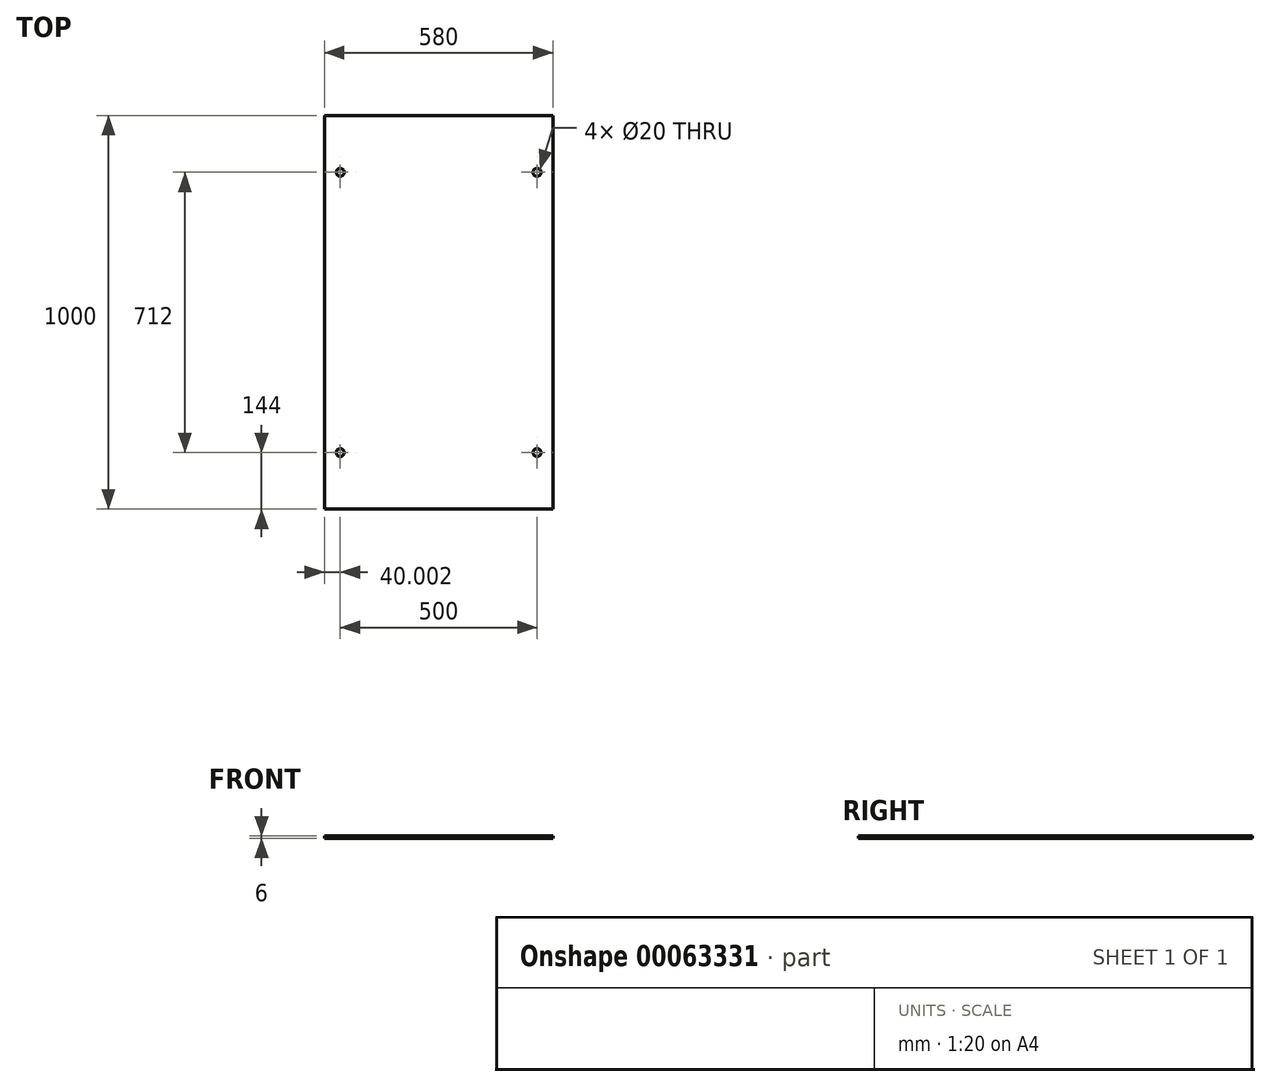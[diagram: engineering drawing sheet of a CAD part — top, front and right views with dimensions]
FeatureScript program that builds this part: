
annotation { "Feature Type Name" : "Feature", "Feature Type Description" : "" }
export const myFeature = defineFeature(function(context is Context, id is Id, definition is map)
    precondition{}
    {
        {
            var Q0;
            Q0=qCreatedBy(makeId("Top.planeOp"),FACE);
            var sketch = newSketch(context, id + "F0", { "sketchPlane" : qUnion([Q0])});
            skLineSegment(sketch, "E0.rect.bottom", {"start": v(293.63, -500) * mm, "end": v(-286.37, -500) * mm});
            skLineSegment(sketch, "E0.rect.top", {"start": v(293.63, 500) * mm, "end": v(-286.37, 500) * mm});
            skLineSegment(sketch, "E0.rect.left", {"start": v(293.63, -500) * mm, "end": v(293.63, 500) * mm});
            skLineSegment(sketch, "E0.rect.right", {"start": v(-286.37, -500) * mm, "end": v(-286.37, 500) * mm});
            skPoint(sketch, "E0.rect.middle", {"position": v(3.63, 0) * mm});
            skCircle(sketch, "E1", {"center": v(253.63, 356) * mm, "radius": 10 * mm});
            skCircle(sketch, "E2", {"center": v(253.63, -356) * mm, "radius": 10 * mm});
            skCircle(sketch, "E3", {"center": v(-246.37, 356) * mm, "radius": 10 * mm});
            skCircle(sketch, "E4", {"center": v(-246.37, -356) * mm, "radius": 10 * mm});
            skSolve(sketch);
        }
        {
            var Q0;
            Q0=qSketchRegion(id+"F0",true);
            var Q1;
            Q1=makeQuery(id+"F0.imprint","IMPRINT",FACE,{"disambiguationData":[TD([[makeQuery(id+"F0.imprint","IMPRINT",EDGE,{"derivedFrom":sQuery(id+"F0.wireOp",EDGE,"E0.rect.bottom")}),-1.0]])]});
            extrude(context, id + "F1", {"entities" : qUnion([Q0, Q1]), "depth" : 6 * mm});
        }
    });
